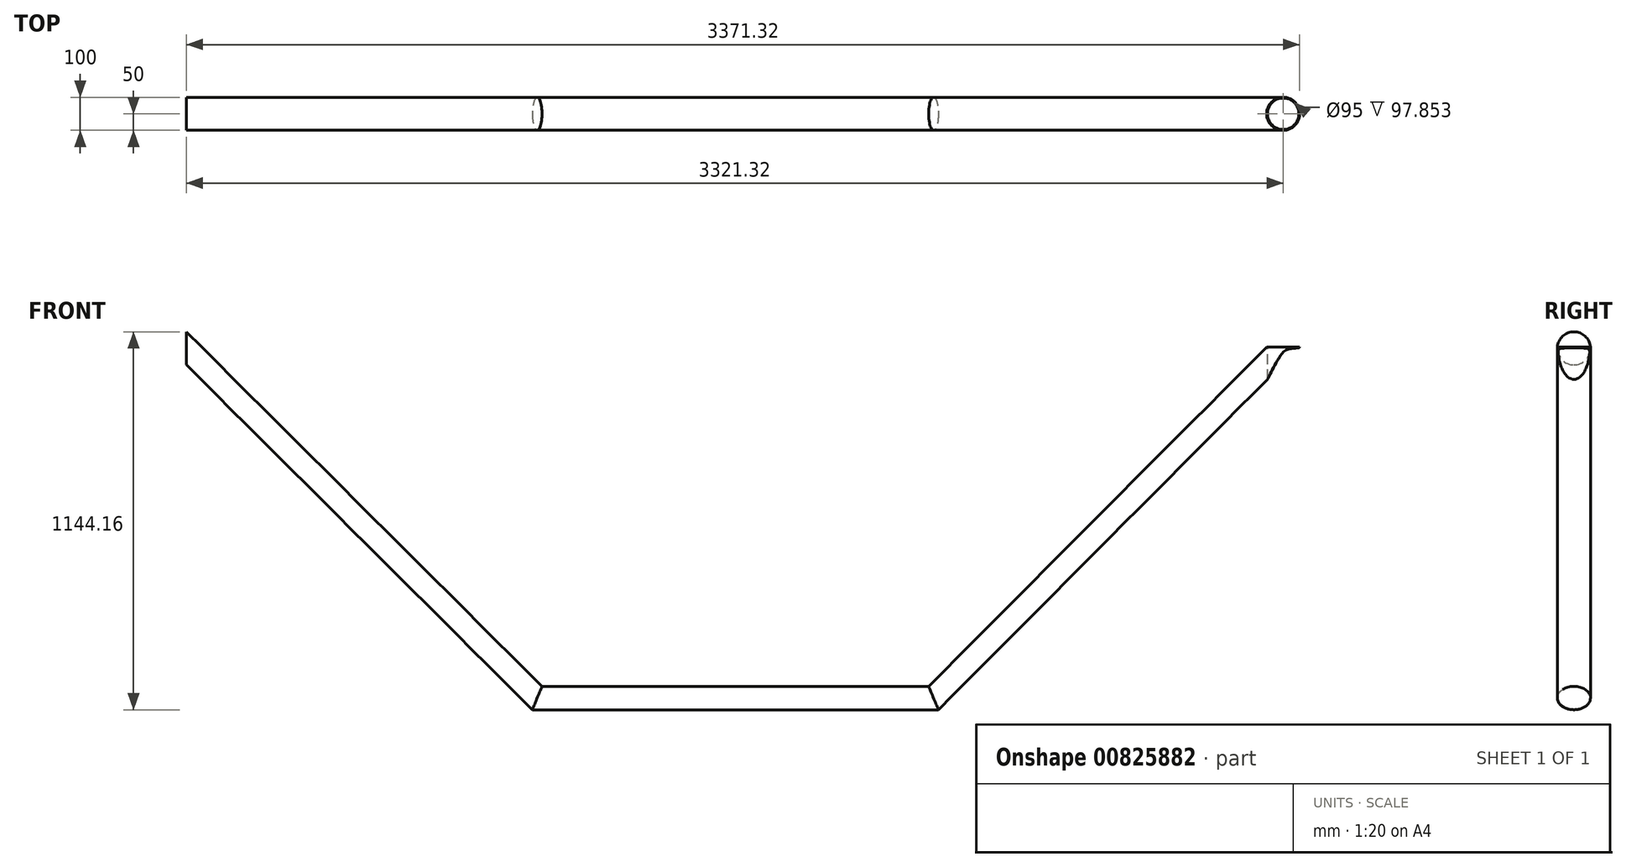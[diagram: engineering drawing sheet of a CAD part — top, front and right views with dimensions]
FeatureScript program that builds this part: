
annotation { "Feature Type Name" : "Feature", "Feature Type Description" : "" }
export const myFeature = defineFeature(function(context is Context, id is Id, definition is map)
    precondition{}
    {
        {
            var Q0;
            Q0=qCreatedBy(makeId("Right.planeOp"),FACE);
            var sketch = newSketch(context, id + "F0", { "sketchPlane" : qUnion([Q0])});
            skCircle(sketch, "E0", {"center": v(0, 0) * mm, "radius": 50 * mm});
            skSolve(sketch);
        }
        {
            var Q0;
            Q0=qCreatedBy(makeId("Front.planeOp"),FACE);
            var sketch = newSketch(context, id + "F1", { "sketchPlane" : qUnion([Q0])});
            skLineSegment(sketch, "E1", {"start": v(0, 0) * mm, "end": v(1062.57, -1058.74) * mm});
            skLineSegment(sketch, "E2", {"start": v(1062.57, -1058.74) * mm, "end": v(2262.57, -1058.74) * mm});
            skLineSegment(sketch, "E3", {"start": v(2262.57, -1058.74) * mm, "end": v(3321.32, 3.83) * mm});
            skSolve(sketch);
        }
        {
            var Q0;
            Q0=makeQuery(id+"F0.imprint","IMPRINT",FACE,{"disambiguationData":[TD([[makeQuery(id+"F0.imprint","IMPRINT",EDGE,{"derivedFrom":sQuery(id+"F0.wireOp",EDGE,"E0")}),1.0]])]});
            var Q1;
            Q1=sQuery(id+"F1.wireOp",EDGE,"E1");
            var Q2;
            Q2=sQuery(id+"F1.wireOp",EDGE,"E2");
            var Q3;
            Q3=sQuery(id+"F1.wireOp",EDGE,"E3");
            sweep(context, id + "F2", {"profiles" : qUnion([Q0]), "path" : qUnion([Q1, Q2, Q3])});
        }
        {
            var Q0;
            Q0=makeQuery(id+"F2.opSweep","CAP_FACE",FACE,{"disambiguationData":[OSD([sQuery(id+"F0.wireOp",EDGE,"E0"),sQuery(id+"F1.wireOp",VERTEX,"E3.end")])],"isStart":false});
            var sketch = newSketch(context, id + "F3", { "sketchPlane" : qUnion([Q0])});
            skPoint(sketch, "E4", {"position": v(3321.32, 0) * mm});
            skSolve(sketch);
        }
        {
            var Q0;
            Q0=sQuery(id+"F3.wireOp",VERTEX,"E4");
            var Q1;
            Q1=makeQuery(id+"F2.opSweep","SWEPT_BODY",BODY,{"disambiguationData":[OSD([sQuery(id+"F0.wireOp",EDGE,"E0"),sQuery(id+"F1.wireOp",EDGE,"E3")])]});
            hole(context, id + "F4", {"style" : HoleStyle.SIMPLE, "endStyle" : HoleEndStyle.THROUGH, "holeDiameter" : 95 * mm, "majorDiameter" : 5 * mm, "isTappedThrough" : true, "tappedDepth" : 12 * mm, "tapClearance" : 3, "locations" : qUnion([Q0]), "scope" : qUnion([Q1])});
        }
    });
